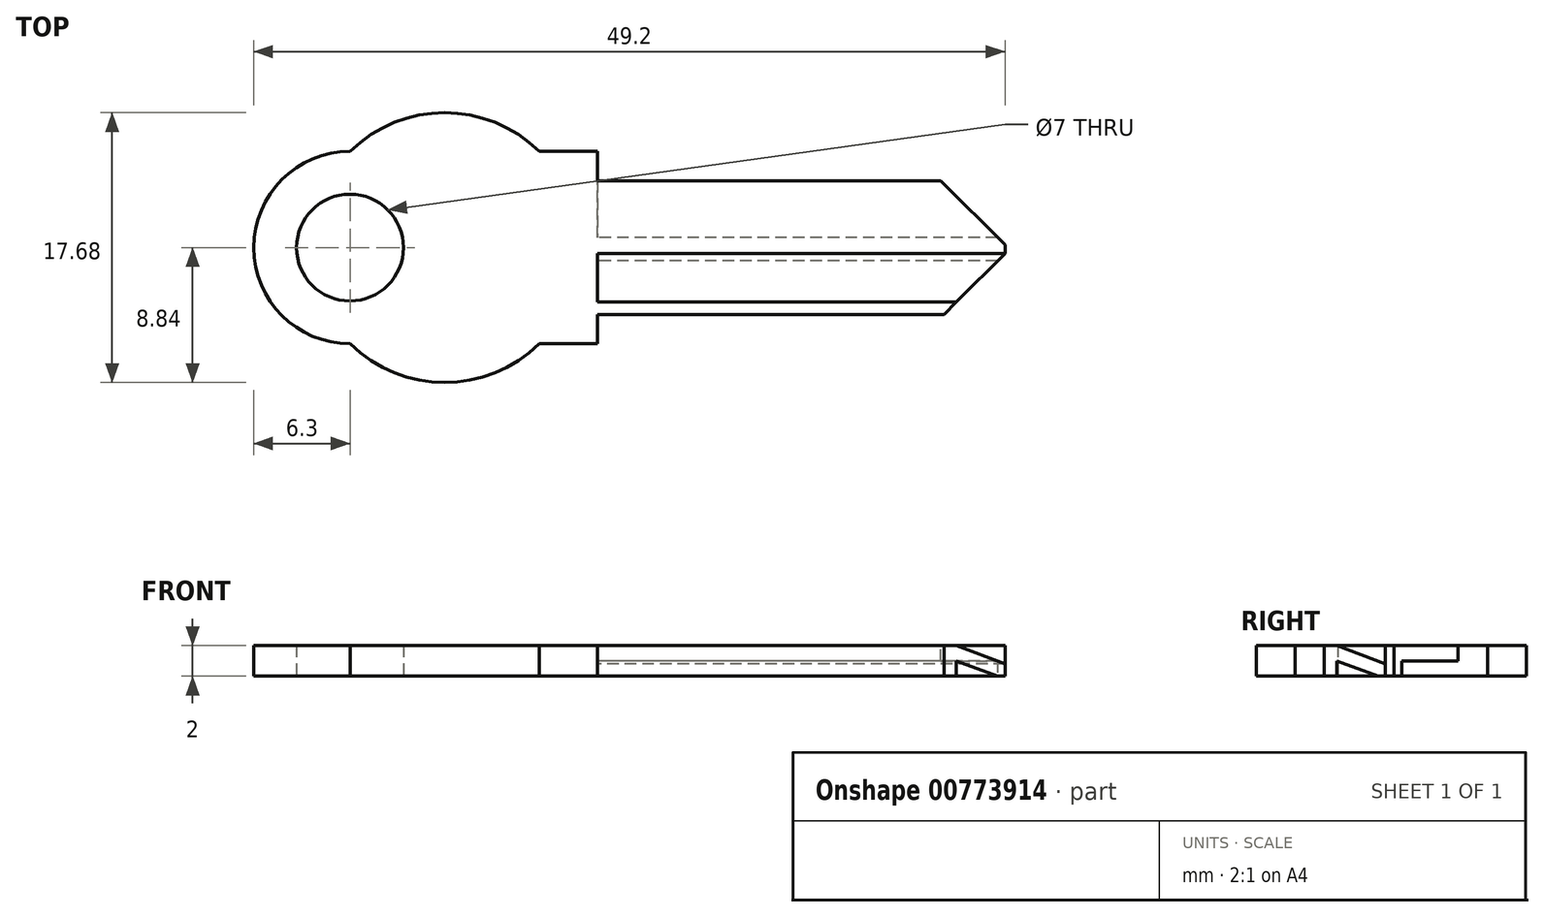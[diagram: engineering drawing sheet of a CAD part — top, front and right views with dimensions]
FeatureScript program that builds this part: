
annotation { "Feature Type Name" : "Feature", "Feature Type Description" : "" }
export const myFeature = defineFeature(function(context is Context, id is Id, definition is map)
    precondition{}
    {
        {
            var Q0;
            Q0=qCreatedBy(makeId("Top.planeOp"),FACE);
            var sketch = newSketch(context, id + "F0", { "sketchPlane" : qUnion([Q0])});
            skLineSegment(sketch, "E0.bottom", {"start": v(10, -6.3) * mm, "end": v(6.2, -6.3) * mm});
            skLineSegment(sketch, "E0.top", {"start": v(10, 6.3) * mm, "end": v(6.2, 6.3) * mm});
            skLineSegment(sketch, "E0.left", {"start": v(10, -6.3) * mm, "end": v(10, 6.3) * mm});
            skPoint(sketch, "E0.middle", {"position": v(0, 0) * mm});
            skArc(sketch, "E1", {"start": v(-6.2, 6.3) * mm, "mid": v(-12.5, 0) * mm, "end": v(-6.2, -6.3) * mm});
            skPoint(sketch, "E2", {"position": v(-10, 0) * mm});
            skPoint(sketch, "E3.orphan", {"position": v(-10, 6.3) * mm});
            skPoint(sketch, "E4.orphan", {"position": v(-10, -6.3) * mm});
            skArc(sketch, "E5", {"start": v(6.2, 6.3) * mm, "mid": v(0, 8.84) * mm, "end": v(-6.2, 6.3) * mm});
            skArc(sketch, "E6.trimOffspring", {"start": v(-6.2, -6.3) * mm, "mid": v(0, -8.84) * mm, "end": v(6.2, -6.3) * mm});
            skCircle(sketch, "E7", {"center": v(-6.2, 0) * mm, "radius": 3.5 * mm});
            skSolve(sketch);
        }
        {
            var Q0;
            Q0=qSketchRegion(id+"F0",true);
            extrude(context, id + "F1", {"entities" : qUnion([Q0]), "depth" : 2 * mm, "offsetDistance" : 25 * mm});
        }
        {
            var Q0;
            Q0=makeQuery(id+"F1.opExtrude","SWEPT_FACE",FACE,{"disambiguationData":[OSD([sQuery(id+"F0.wireOp",EDGE,"E0.left")])]});
            var sketch = newSketch(context, id + "F2", { "sketchPlane" : qUnion([Q0])});
            skLineSegment(sketch, "E8.bottom", {"start": v(0.68, 0) * mm, "end": v(-0.88, 0) * mm});
            skLineSegment(sketch, "E8.top", {"start": v(4.38, 2) * mm, "end": v(-0.38, 2) * mm});
            skLineSegment(sketch, "E8.left", {"start": v(4.38, 1) * mm, "end": v(4.38, 2) * mm});
            skLineSegment(sketch, "E8.right", {"start": v(-4.38, 0) * mm, "end": v(-4.38, 2) * mm});
            skLineSegment(sketch, "E9", {"start": v(4.38, 1) * mm, "end": v(0.68, 1) * mm});
            skLineSegment(sketch, "E10", {"start": v(0.68, 1) * mm, "end": v(0.68, 0) * mm});
            skPoint(sketch, "E11.orphan", {"position": v(4.38, 0) * mm});
            skLineSegment(sketch, "E12", {"start": v(-3.58, 0) * mm, "end": v(-3.58, 1) * mm});
            skLineSegment(sketch, "E13", {"start": v(-3.58, 1) * mm, "end": v(-0.87, 0) * mm});
            skLineSegment(sketch, "E14", {"start": v(-0.38, 2) * mm, "end": v(-0.38, 0.8) * mm});
            skLineSegment(sketch, "E15", {"start": v(-0.38, 0.8) * mm, "end": v(-3.58, 2) * mm});
            skLineSegment(sketch, "E16.trimOffspring", {"start": v(-3.58, 2) * mm, "end": v(-4.38, 2) * mm});
            skLineSegment(sketch, "E17.trimOffspring", {"start": v(-3.58, 0) * mm, "end": v(-4.38, 0) * mm});
            skSolve(sketch);
        }
        {
            var Q0;
            Q0=qSketchRegion(id+"F2",true);
            extrude(context, id + "F3", {"entities" : qUnion([Q0]), "operationType" : NewBodyOperationType.ADD, "depth" : 26.7 * mm, "offsetDistance" : 25 * mm});
        }
        {
            var Q0;
            Q0=makeQuery(id+"F3.boolean.opBoolean","MERGE",FACE,{"derivedFrom":[makeQuery(id+"F1.opExtrude","CAP_FACE",FACE,{"disambiguationData":[OSD([sQuery(id+"F0.wireOp",EDGE,"E0.bottom"),sQuery(id+"F0.wireOp",EDGE,"E0.top"),sQuery(id+"F0.wireOp",EDGE,"E0.left"),sQuery(id+"F0.wireOp",EDGE,"E1"),sQuery(id+"F0.wireOp",EDGE,"E5"),sQuery(id+"F0.wireOp",EDGE,"E6.trimOffspring"),sQuery(id+"F0.wireOp",EDGE,"E7")])],"isStart":false}),makeQuery(id+"F3.opExtrude","SWEPT_FACE",FACE,{"disambiguationData":[OSD([sQuery(id+"F2.wireOp",EDGE,"E8.top")])]}),makeQuery(id+"F3.opExtrude","SWEPT_FACE",FACE,{"disambiguationData":[OSD([sQuery(id+"F2.wireOp",EDGE,"E16.trimOffspring")])]})]});
            var sketch = newSketch(context, id + "F4", { "sketchPlane" : qUnion([Q0])});
            skPoint(sketch, "E18.orphan", {"position": v(10, -4.38) * mm});
            skPoint(sketch, "E19.orphan", {"position": v(10, 4.38) * mm});
            skLineSegment(sketch, "E20.0", {"start": v(36.7, 4.38) * mm, "end": v(10, 4.38) * mm, "construction": true});
            skLineSegment(sketch, "E21.0", {"start": v(36.7, -0.38) * mm, "end": v(36.7, 4.38) * mm, "construction": true});
            skLineSegment(sketch, "E22.0", {"start": v(36.7, -4.38) * mm, "end": v(36.7, -3.57) * mm, "construction": true});
            skLineSegment(sketch, "E23.0", {"start": v(36.7, -4.38) * mm, "end": v(10, -4.38) * mm, "construction": true});
            skLineSegment(sketch, "E24", {"start": v(36.7, 4.38) * mm, "end": v(36.7, 0.17) * mm});
            skLineSegment(sketch, "E25", {"start": v(36.7, 0.18) * mm, "end": v(32.5, 4.38) * mm});
            skLineSegment(sketch, "E26", {"start": v(32.5, 4.38) * mm, "end": v(36.7, 4.38) * mm});
            skLineSegment(sketch, "E27", {"start": v(36.7, -4.38) * mm, "end": v(36.7, -0.38) * mm});
            skLineSegment(sketch, "E28", {"start": v(36.7, -4.38) * mm, "end": v(32.7, -4.38) * mm});
            skLineSegment(sketch, "E29", {"start": v(32.7, -4.38) * mm, "end": v(36.7, -0.38) * mm});
            skSolve(sketch);
        }
        {
            var Q0;
            Q0=qSketchRegion(id+"F4",true);
            extrude(context, id + "F5", {"entities" : qUnion([Q0]), "operationType" : NewBodyOperationType.REMOVE, "endBound" : BoundingType.THROUGH_ALL, "oppositeDirection" : true, "depth" : 25 * mm, "offsetDistance" : 25 * mm});
        }
    });
